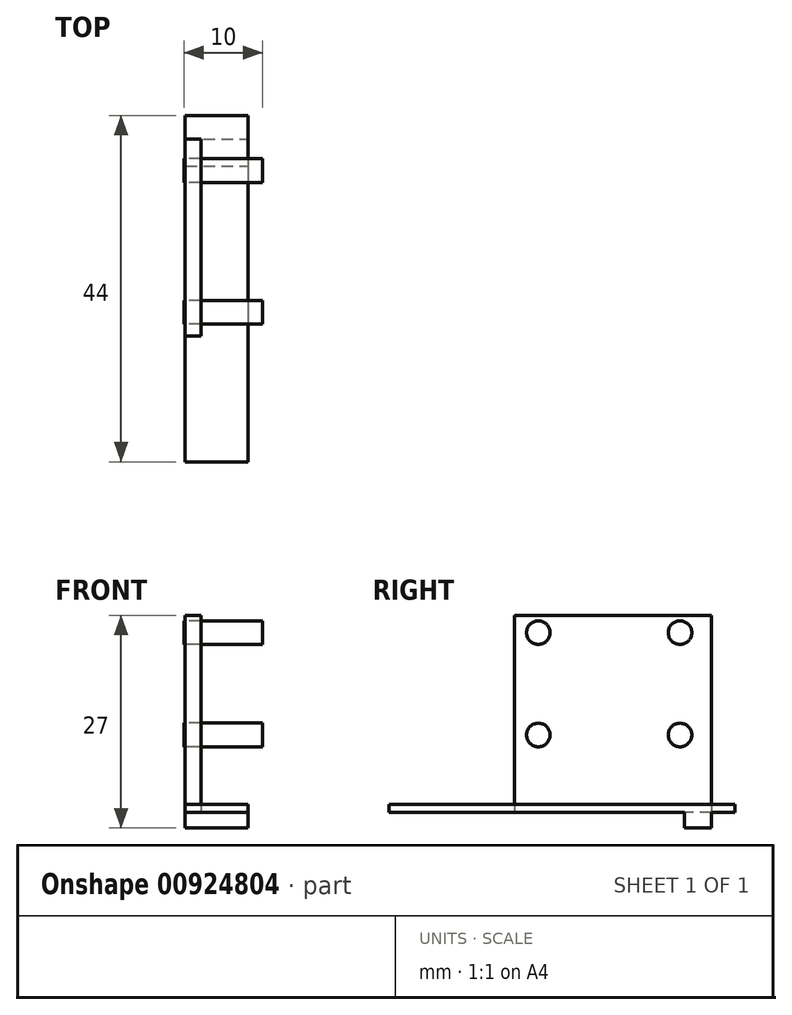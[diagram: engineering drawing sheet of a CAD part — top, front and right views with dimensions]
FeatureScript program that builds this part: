
annotation { "Feature Type Name" : "Feature", "Feature Type Description" : "" }
export const myFeature = defineFeature(function(context is Context, id is Id, definition is map)
    precondition{}
    {
        {
            var Q0;
            Q0=qCreatedBy(makeId("Top.planeOp"),FACE);
            var sketch = newSketch(context, id + "F0", { "sketchPlane" : qUnion([Q0])});
            skLineSegment(sketch, "E0.bottom", {"start": v(0.15, 40.87) * mm, "end": v(8.15, 40.87) * mm});
            skLineSegment(sketch, "E0.top", {"start": v(0.15, -3.13) * mm, "end": v(8.15, -3.13) * mm});
            skLineSegment(sketch, "E0.left", {"start": v(0.15, 40.87) * mm, "end": v(0.15, -3.13) * mm});
            skLineSegment(sketch, "E0.right", {"start": v(8.15, 40.87) * mm, "end": v(8.15, -3.13) * mm});
            skLineSegment(sketch, "E1.bottom", {"start": v(0.15, 40.87) * mm, "end": v(4, 40.87) * mm});
            skLineSegment(sketch, "E2", {"start": v(0.15, 37.87) * mm, "end": v(8.15, 37.87) * mm});
            skLineSegment(sketch, "E3", {"start": v(0.15, 34.46) * mm, "end": v(8.15, 34.46) * mm});
            skLineSegment(sketch, "E4", {"start": v(2.15, 37.87) * mm, "end": v(2.15, 12.87) * mm});
            skLineSegment(sketch, "E5", {"start": v(2.15, 12.87) * mm, "end": v(0.15, 12.87) * mm});
            skSolve(sketch);
        }
        {
            var Q0;
            {var subQ0=sQuery(id+"F0.wireOp",EDGE,"E3");var subQ1=sQuery(id+"F0.wireOp",EDGE,"E0.right");var subQ2=makeQuery(id+"F0.imprint","INTERSECT",VERTEX,{"derivedFrom":[subQ1,subQ0]});Q0=makeQuery(id+"F0.imprint","IMPRINT",FACE,{"disambiguationData":[TD([[makeQuery(id+"F0.imprint","IMPRINT",EDGE,{"disambiguationData":[TD([[subQ2,1.0]])],"derivedFrom":subQ1}),-1.0]])]});}
            var Q1;
            {var subQ0=sQuery(id+"F0.wireOp",EDGE,"E3");var subQ1=sQuery(id+"F0.wireOp",EDGE,"E0.left");var subQ2=makeQuery(id+"F0.imprint","INTERSECT",VERTEX,{"derivedFrom":[subQ1,subQ0]});Q1=makeQuery(id+"F0.imprint","IMPRINT",FACE,{"disambiguationData":[TD([[makeQuery(id+"F0.imprint","IMPRINT",EDGE,{"disambiguationData":[TD([[subQ2,1.0]])],"derivedFrom":subQ1}),1.0]])]});}
            extrude(context, id + "F1", {"entities" : qUnion([Q0, Q1]), "oppositeDirection" : true, "depth" : 2 * mm, "offsetDistance" : 25 * mm});
        }
        {
            var Q0;
            {var subQ1=sQuery(id+"F0.wireOp",EDGE,"E0.top");Q0=makeQuery(id+"F0.imprint","IMPRINT",FACE,{"disambiguationData":[TD([[makeQuery(id+"F0.imprint","IMPRINT",EDGE,{"derivedFrom":subQ1}),1.0]])]});}
            var Q1;
            {var subQ0=sQuery(id+"F0.wireOp",EDGE,"E3");var subQ1=sQuery(id+"F0.wireOp",EDGE,"E0.left");var subQ2=makeQuery(id+"F0.imprint","INTERSECT",VERTEX,{"derivedFrom":[subQ1,subQ0]});Q1=makeQuery(id+"F0.imprint","IMPRINT",FACE,{"disambiguationData":[TD([[makeQuery(id+"F0.imprint","IMPRINT",EDGE,{"disambiguationData":[TD([[subQ2,1.0]])],"derivedFrom":subQ1}),1.0]])]});}
            var Q2;
            {var subQ0=sQuery(id+"F0.wireOp",EDGE,"E3");var subQ1=sQuery(id+"F0.wireOp",EDGE,"E0.right");var subQ2=makeQuery(id+"F0.imprint","INTERSECT",VERTEX,{"derivedFrom":[subQ1,subQ0]});Q2=makeQuery(id+"F0.imprint","IMPRINT",FACE,{"disambiguationData":[TD([[makeQuery(id+"F0.imprint","IMPRINT",EDGE,{"disambiguationData":[TD([[subQ2,1.0]])],"derivedFrom":subQ1}),-1.0]])]});}
            var Q3;
            {var subQ4=sQuery(id+"F0.wireOp",EDGE,"E0.bottom");Q3=makeQuery(id+"F0.imprint","IMPRINT",FACE,{"disambiguationData":[TD([[makeQuery(id+"F0.imprint","IMPRINT",EDGE,{"derivedFrom":subQ4}),-1.0]])]});}
            var Q4;
            {var subQ3=sQuery(id+"F0.wireOp",EDGE,"E5");Q4=makeQuery(id+"F0.imprint","IMPRINT",FACE,{"disambiguationData":[TD([[makeQuery(id+"F0.imprint","IMPRINT",EDGE,{"derivedFrom":subQ3}),-1.0]])]});}
            extrude(context, id + "F2", {"entities" : qUnion([Q0, Q1, Q2, Q3, Q4]), "operationType" : NewBodyOperationType.ADD, "depth" : 1 * mm, "offsetDistance" : 25 * mm});
        }
        {
            var Q0;
            {var subQ0=sQuery(id+"F0.wireOp",EDGE,"E3");var subQ1=sQuery(id+"F0.wireOp",EDGE,"E0.left");var subQ2=makeQuery(id+"F0.imprint","INTERSECT",VERTEX,{"derivedFrom":[subQ1,subQ0]});Q0=makeQuery(id+"F0.imprint","IMPRINT",FACE,{"disambiguationData":[TD([[makeQuery(id+"F0.imprint","IMPRINT",EDGE,{"disambiguationData":[TD([[subQ2,1.0]])],"derivedFrom":subQ1}),1.0]])]});}
            var Q1;
            {var subQ3=sQuery(id+"F0.wireOp",EDGE,"E5");Q1=makeQuery(id+"F0.imprint","IMPRINT",FACE,{"disambiguationData":[TD([[makeQuery(id+"F0.imprint","IMPRINT",EDGE,{"derivedFrom":subQ3}),-1.0]])]});}
            extrude(context, id + "F3", {"entities" : qUnion([Q0, Q1]), "depth" : 25 * mm, "offsetDistance" : 25 * mm});
        }
        {
            var Q0;
            Q0=qCreatedBy(makeId("Right.planeOp"),FACE);
            var sketch = newSketch(context, id + "F4", { "sketchPlane" : qUnion([Q0])});
            skCircle(sketch, "E6", {"center": v(15.87, 9.82) * mm, "radius": 1.5 * mm});
            skCircle(sketch, "E7", {"center": v(33.87, 9.82) * mm, "radius": 1.5 * mm});
            skCircle(sketch, "E8", {"center": v(15.87, 22.82) * mm, "radius": 1.5 * mm});
            skCircle(sketch, "E9", {"center": v(33.87, 22.82) * mm, "radius": 1.5 * mm});
            skSolve(sketch);
        }
        {
            var Q0;
            Q0=makeQuery(id+"F4.imprint","IMPRINT",FACE,{"disambiguationData":[TD([[makeQuery(id+"F4.imprint","IMPRINT",EDGE,{"derivedFrom":sQuery(id+"F4.wireOp",EDGE,"E6")}),1.0]])]});
            var Q1;
            Q1=makeQuery(id+"F4.imprint","IMPRINT",FACE,{"disambiguationData":[TD([[makeQuery(id+"F4.imprint","IMPRINT",EDGE,{"derivedFrom":sQuery(id+"F4.wireOp",EDGE,"E8")}),1.0]])]});
            var Q2;
            Q2=makeQuery(id+"F4.imprint","IMPRINT",FACE,{"disambiguationData":[TD([[makeQuery(id+"F4.imprint","IMPRINT",EDGE,{"derivedFrom":sQuery(id+"F4.wireOp",EDGE,"E9")}),1.0]])]});
            var Q3;
            Q3=makeQuery(id+"F4.imprint","IMPRINT",FACE,{"disambiguationData":[TD([[makeQuery(id+"F4.imprint","IMPRINT",EDGE,{"derivedFrom":sQuery(id+"F4.wireOp",EDGE,"E7")}),1.0]])]});
            extrude(context, id + "F5", {"entities" : qUnion([Q0, Q1, Q2, Q3]), "depth" : 10 * mm, "offsetDistance" : 25 * mm});
        }
    });
